# Revit family: DONE-2019_Valvula_Arco_Turia
name_source: partatom
category: Pipe Accessories
units: mm (PartAtom-declared; Revit-internal decimal feet)

## family parameters
Always vertical = Yes
Cut with Voids When Loaded = No
OmniClass Number = 23.65.55.14.21
OmniClass Title = Non-Return Valves for Liquid Services
Part Type = Valve - Breaks Into
Round Connector Dimension = Use Radius
Shared = No
Work Plane-Based = No

## types (1)
- DONE-2019_Valvula_Arco_Turia
    A = 82 mm  [stored 0.269029 ft]
    Ancho Símbolo = 15 mm  [stored 0.0492126 ft]
    B = 112 mm  [stored 0.367454 ft]
    C = 90 mm  [stored 0.295276 ft]
    Cost = €5.80
    D = 32 mm
    Description = Válvula esfera Turia mando palanca H-H
    Diámetro Exterior = 45 mm
    Diámetro Nominal = 32 mm
    E = 32 mm
    HEX = Yes
    K Coefficient = 0.35
    Manufacturer = Vávulas Arco S.L
    Material = Jatón Europeo CW617N - Chromado
    OCT = No
    Radio Cuerpo = 26 mm
    Radio Exterior = 22 mm
    Radio Nominal = 16 mm
    Radio Tuerca = 23 mm
    URL = www.valvulasarco.com

note: [stored X ft] marks values corroborated as IEEE doubles in the binary element streams (Revit-internal decimal feet)

## geometry (parser evidence)
native form markers: Sweep x2
no freeform markers — native parametric forms only
